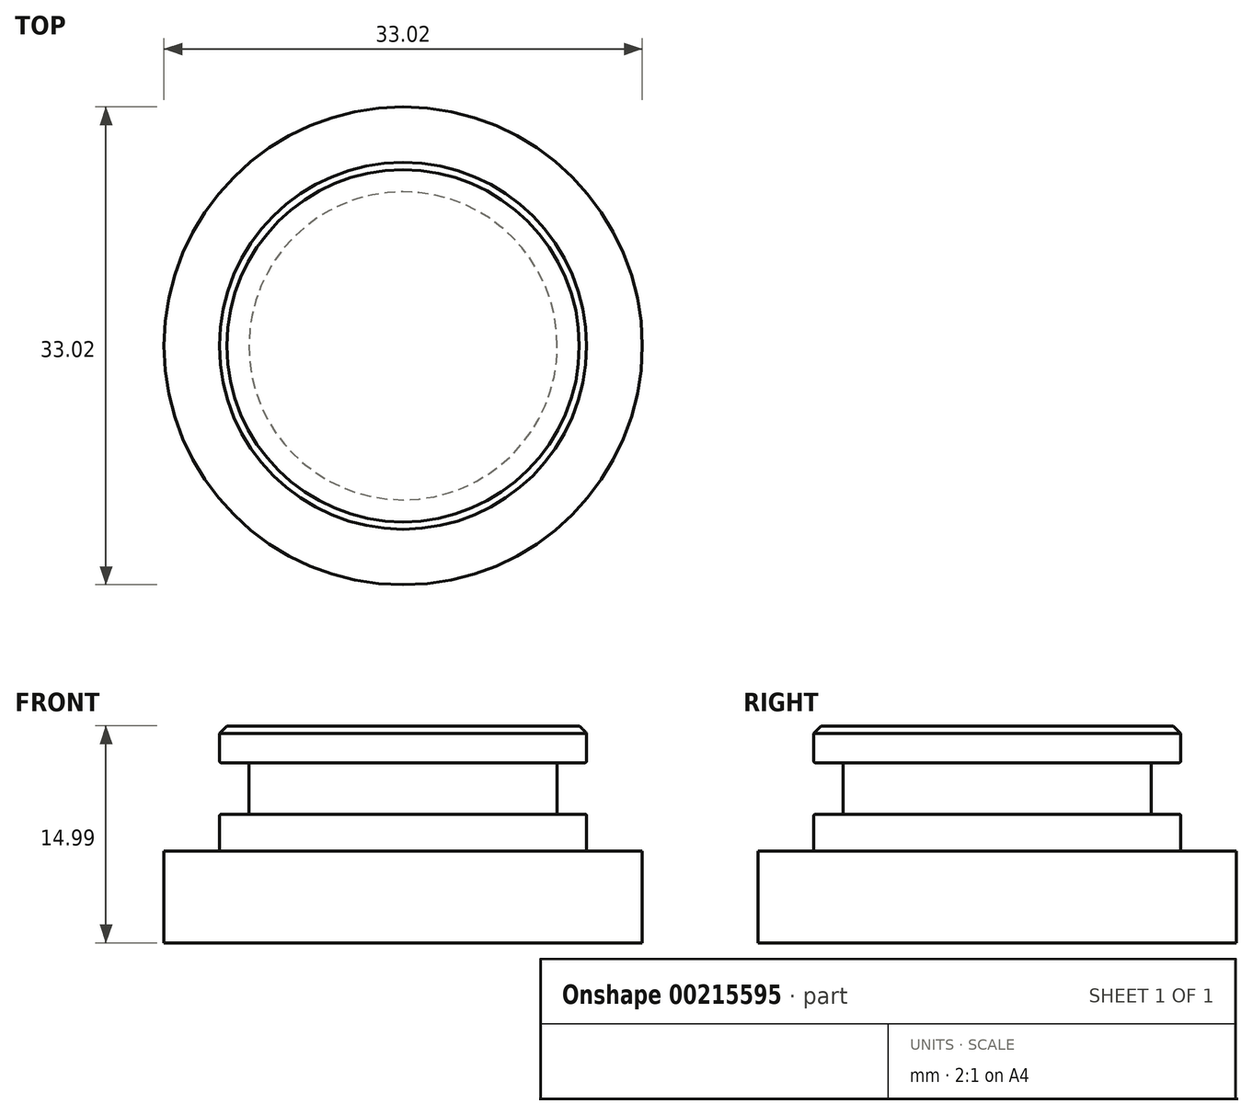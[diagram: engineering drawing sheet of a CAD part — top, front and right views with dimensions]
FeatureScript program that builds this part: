
annotation { "Feature Type Name" : "Feature", "Feature Type Description" : "" }
export const myFeature = defineFeature(function(context is Context, id is Id, definition is map)
    precondition{}
    {
        {
            var Q0;
            Q0=qCreatedBy(makeId("Top.planeOp"),FACE);
            var sketch = newSketch(context, id + "F0", { "sketchPlane" : qUnion([Q0])});
            skCircle(sketch, "E0", {"center": v(0, 0) * mm, "radius": 16.51 * mm});
            skSolve(sketch);
        }
        {
            var Q0;
            Q0 = qSketchRegion(id + "F0", true);
            extrude(context, id + "F1", {"entities" : qUnion([Q0]), "depth" : 6.35 * mm});
        }
        {
            var Q0;
            Q0=makeQuery(id+"F1.opExtrude","CAP_FACE",FACE,{"disambiguationData":[OSD([sQuery(id+"F0.wireOp",EDGE,"E0")])],"isStart":false});
            var sketch = newSketch(context, id + "F2", { "sketchPlane" : qUnion([Q0])});
            skCircle(sketch, "E1", {"center": v(0, 0) * mm, "radius": 12.67 * mm});
            skSolve(sketch);
        }
        {
            var Q0;
            Q0 = qSketchRegion(id + "F2", true);
            extrude(context, id + "F3", {"entities" : qUnion([Q0]), "operationType" : NewBodyOperationType.ADD, "depth" : 2.54 * mm});
        }
        {
            var Q0;
            Q0=makeQuery(id+"F3.opExtrude","CAP_FACE",FACE,{"disambiguationData":[OSD([sQuery(id+"F2.wireOp",EDGE,"E1")])],"isStart":false});
            var sketch = newSketch(context, id + "F4", { "sketchPlane" : qUnion([Q0])});
            skCircle(sketch, "E2", {"center": v(0, 0) * mm, "radius": 10.64 * mm});
            skSolve(sketch);
        }
        {
            var Q0;
            Q0 = qSketchRegion(id + "F4", true);
            extrude(context, id + "F5", {"entities" : qUnion([Q0]), "operationType" : NewBodyOperationType.ADD, "depth" : 3.56 * mm});
        }
        {
            var Q0;
            Q0=makeQuery(id+"F5.opExtrude","CAP_FACE",FACE,{"disambiguationData":[OSD([sQuery(id+"F4.wireOp",EDGE,"E2")])],"isStart":false});
            var sketch = newSketch(context, id + "F6", { "sketchPlane" : qUnion([Q0])});
            skCircle(sketch, "E3", {"center": v(0, 0) * mm, "radius": 12.67 * mm});
            skSolve(sketch);
        }
        {
            var Q0;
            Q0 = qSketchRegion(id + "F6", true);
            extrude(context, id + "F7", {"entities" : qUnion([Q0]), "operationType" : NewBodyOperationType.ADD, "depth" : 2.54 * mm});
        }
        {
            var Q0;
            Q0=makeQuery(id+"F5.opExtrude","CAP_EDGE",EDGE,{"disambiguationData":[OSD([sQuery(id+"F4.wireOp",EDGE,"E2")])],"isStart":true});
            var Q1;
            Q1=makeQuery(id+"F3.opExtrude","CAP_EDGE",EDGE,{"disambiguationData":[OSD([sQuery(id+"F2.wireOp",EDGE,"E1")])],"isStart":false});
            var Q2;
            Q2=makeQuery(id+"F7.opExtrude","CAP_EDGE",EDGE,{"disambiguationData":[OSD([sQuery(id+"F6.wireOp",EDGE,"E3")])],"isStart":true});
            var Q3;
            Q3=makeQuery(id+"F5.opExtrude","CAP_EDGE",EDGE,{"disambiguationData":[OSD([sQuery(id+"F4.wireOp",EDGE,"E2")])],"isStart":false});
            fillet(context, id + "F8", {"entities" : qUnion([Q0, Q1, Q2, Q3]), "radius" : 0.13 * mm, "tangentPropagation" : true, "allowEdgeOverflow" : false});
        }
        {
            var Q0;
            Q0=makeQuery(id+"F7.opExtrude","CAP_EDGE",EDGE,{"disambiguationData":[OSD([sQuery(id+"F6.wireOp",EDGE,"E3")])],"isStart":false});
            chamfer(context, id + "F9", {"entities" : qUnion([Q0]), "width" : 0.5 * mm, "tangentPropagation" : true});
        }
    });
